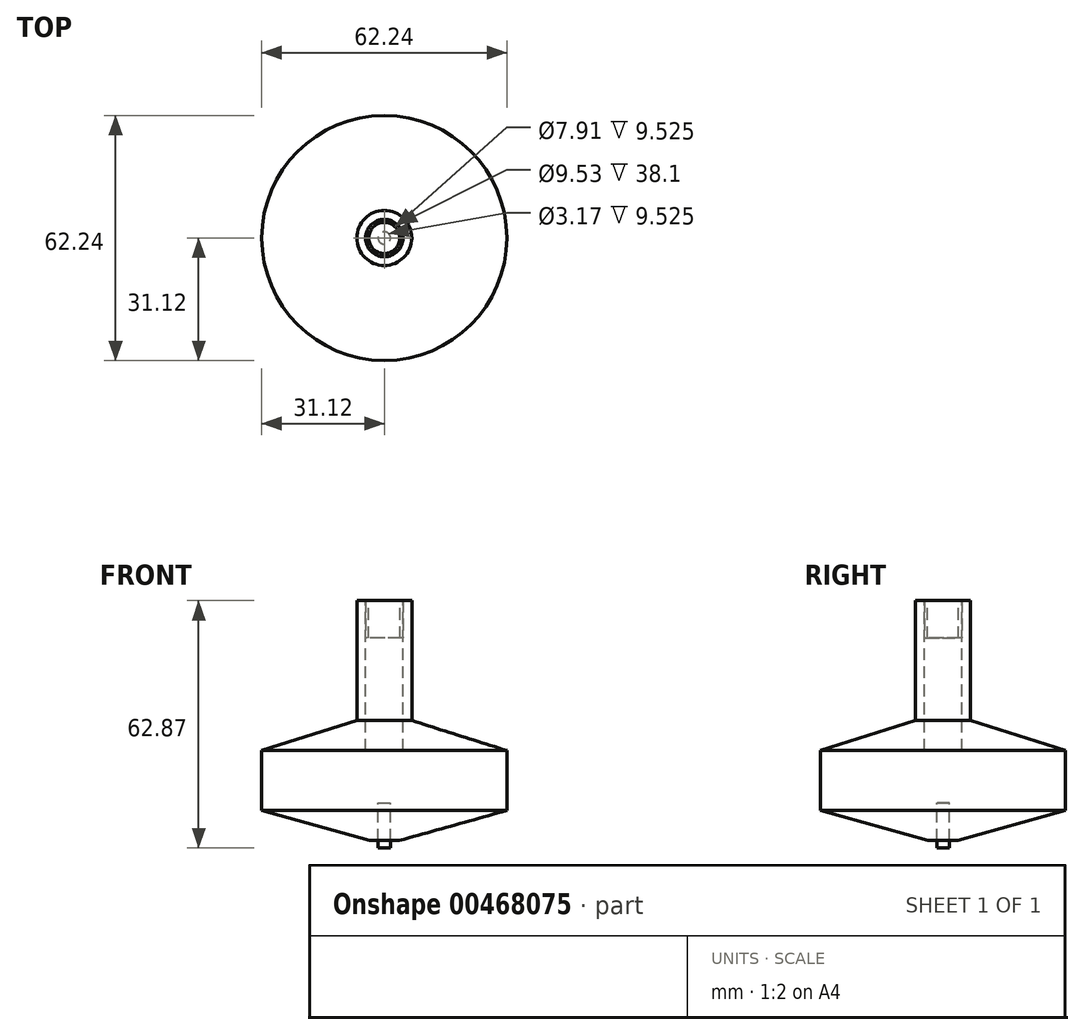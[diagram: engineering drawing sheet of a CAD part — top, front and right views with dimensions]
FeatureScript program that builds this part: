
annotation { "Feature Type Name" : "Feature", "Feature Type Description" : "" }
export const myFeature = defineFeature(function(context is Context, id is Id, definition is map)
    precondition{}
    {
        {
            var Q0;
            Q0=qCreatedBy(makeId("Front.planeOp"),FACE);
            var sketch = newSketch(context, id + "F0", { "sketchPlane" : qUnion([Q0])});
            skLineSegment(sketch, "E0", {"start": v(31.12, 9.53) * mm, "end": v(31.12, 24.77) * mm});
            skLineSegment(sketch, "E1", {"start": v(6.98, 62.87) * mm, "end": v(0, 62.87) * mm});
            skLineSegment(sketch, "E2", {"start": v(0, 62.87) * mm, "end": v(0, 1.9) * mm});
            skLineSegment(sketch, "E3", {"start": v(0, 1.9) * mm, "end": v(3.81, 1.9) * mm});
            skLineSegment(sketch, "E4", {"start": v(3.81, 1.9) * mm, "end": v(31.12, 9.53) * mm});
            skLineSegment(sketch, "E5", {"start": v(31.12, 24.77) * mm, "end": v(6.98, 32.39) * mm});
            skLineSegment(sketch, "E6", {"start": v(6.98, 32.39) * mm, "end": v(6.98, 62.87) * mm});
            skPoint(sketch, "E7", {"position": v(31.12, 17.15) * mm});
            skSolve(sketch);
        }
        {
            var Q0;
            Q0=makeQuery(id+"F0.imprint","IMPRINT",FACE,{"disambiguationData":[TD([[makeQuery(id+"F0.imprint","IMPRINT",EDGE,{"derivedFrom":sQuery(id+"F0.wireOp",EDGE,"E0")}),1.0]])]});
            var Q1;
            Q1=sQuery(id+"F0.wireOp",EDGE,"E2");
            revolve(context, id + "F1", {"entities" : qUnion([Q0]), "axis" : qUnion([Q1]), "revolveType" : RevolveType.FULL});
        }
        {
            var Q0;
            Q0=makeQuery(id+"F1.opRevolve","SWEPT_FACE",FACE,{"disambiguationData":[OSD([sQuery(id+"F0.wireOp",EDGE,"E1")])]});
            var sketch = newSketch(context, id + "F2", { "sketchPlane" : qUnion([Q0])});
            skCircle(sketch, "E8", {"center": v(0, 0) * mm, "radius": 4.76 * mm});
            skSolve(sketch);
        }
        {
            var Q0;
            Q0=makeQuery(id+"F2.imprint","IMPRINT",FACE,{"disambiguationData":[TD([[makeQuery(id+"F2.imprint","IMPRINT",EDGE,{"derivedFrom":sQuery(id+"F2.wireOp",EDGE,"E8")}),1.0]])]});
            extrude(context, id + "F3", {"entities" : qUnion([Q0]), "operationType" : NewBodyOperationType.REMOVE, "oppositeDirection" : true, "depth" : 9.52 * mm});
        }
        {
            var Q0;
            Q0=makeQuery(id+"F1.opRevolve","SWEPT_FACE",FACE,{"disambiguationData":[OSD([sQuery(id+"F0.wireOp",EDGE,"E3")])]});
            var sketch = newSketch(context, id + "F4", { "sketchPlane" : qUnion([Q0])});
            skCircle(sketch, "E9", {"center": v(0, 0) * mm, "radius": 1.59 * mm});
            skSolve(sketch);
        }
        {
            var Q0;
            Q0=qSketchRegion(id+"F4",true);
            extrude(context, id + "F5", {"entities" : qUnion([Q0]), "operationType" : NewBodyOperationType.REMOVE, "oppositeDirection" : true, "depth" : 9.52 * mm});
        }
        {
            var Q0;
            Q0=makeQuery(id+"F3.boolean.opBoolean","COPY",FACE,{"derivedFrom":makeQuery(id+"F3.opExtrude","CAP_FACE",FACE,{"disambiguationData":[OSD([sQuery(id+"F2.wireOp",EDGE,"E8")])],"isStart":false})});
            extrude(context, id + "F6", {"entities" : qUnion([Q0]), "depth" : 9.52 * mm});
        }
        {
            var Q0;
            Q0=makeQuery(id+"F6.opExtrude","CAP_FACE",FACE,{"disambiguationData":[OSD([sQuery(id+"F2.wireOp",EDGE,"E8")])],"isStart":false});
            var sketch = newSketch(context, id + "F7", { "sketchPlane" : qUnion([Q0])});
            skCircle(sketch, "E10", {"center": v(0, 0) * mm, "radius": 3.95 * mm});
            skSolve(sketch);
        }
        {
            var Q0;
            Q0=makeQuery(id+"F7.imprint","IMPRINT",FACE,{"disambiguationData":[TD([[makeQuery(id+"F7.imprint","IMPRINT",EDGE,{"derivedFrom":sQuery(id+"F7.wireOp",EDGE,"E10")}),1.0]])]});
            extrude(context, id + "F8", {"entities" : qUnion([Q0]), "operationType" : NewBodyOperationType.REMOVE, "oppositeDirection" : true, "depth" : 9.52 * mm});
        }
        {
            var Q0;
            Q0=makeQuery(id+"F5.boolean.opBoolean","COPY",FACE,{"derivedFrom":makeQuery(id+"F5.opExtrude","CAP_FACE",FACE,{"disambiguationData":[OSD([sQuery(id+"F4.wireOp",EDGE,"E9")])],"isStart":false})});
            extrude(context, id + "F9", {"entities" : qUnion([Q0]), "depth" : 11.43 * mm});
        }
        {
            var Q0;
            Q0=makeQuery(id+"F3.boolean.opBoolean","COPY",FACE,{"derivedFrom":makeQuery(id+"F3.opExtrude","CAP_FACE",FACE,{"disambiguationData":[OSD([sQuery(id+"F2.wireOp",EDGE,"E8")])],"isStart":false})});
            extrude(context, id + "F10", {"entities" : qUnion([Q0]), "operationType" : NewBodyOperationType.REMOVE, "oppositeDirection" : true, "depth" : 28.57 * mm});
        }
    });
